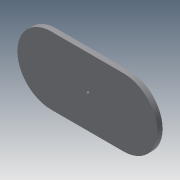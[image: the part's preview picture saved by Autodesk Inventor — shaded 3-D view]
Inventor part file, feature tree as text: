
AUTODESK INVENTOR PART (.ipt)
format: ipt  version: 2013 (Build 170138000, 138)  size: 95,232 bytes
history: native  units: mm
features: extrude x3, sketch x3
ambient origin geometry x8: Origin, YZ Plane, XZ Plane, XY Plane, X Axis, Y Axis, Z Axis, Center Point
bodies: Solid1 (feature_tree)
feature tree (6):
  extrude  "Extrusion1"  Depth=131.0mm
  extrude  "Extrusion2"  Depth=10.0mm TaperAngle=0.0deg
  extrude  "Extrusion3"  Depth=10.0mm TaperAngle=0.0deg
  sketch  "Sketch1"  dims[d0=140.0mm d1=131.0mm]
  sketch  "Sketch2"  dims[d2=15.0mm d3=10.0mm d4=0.0mm]
  sketch  "Sketch3"  dims[d5=6.0mm d6=10.0mm d7=0.0mm d8=10.0mm d9=0.0mm]
